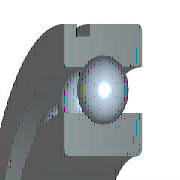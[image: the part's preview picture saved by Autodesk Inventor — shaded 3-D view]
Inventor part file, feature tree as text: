
AUTODESK INVENTOR PART (.ipt)
format: ipt  version: 2015 (Build 190159000, 159)  size: 336,384 bytes
history: native  units: mm (DEFAULTED — no unit token found)
features: sketch x1, other x1, pattern_circular x1
ambient origin geometry x8: Origin, YZ Plane, XZ Plane, XY Plane, X Axis, Y Axis, Z Axis, Center Point
bodies: Solid1 (feature_tree)
feature tree (3):
  sketch  "草图"  dims[d0=4.42mm d17=90.0deg d18=90.0deg d1=0.3mm d2=100.0mm d3=360.0deg d4=0.0mm d5=0.0mm d6=0.0mm d7=20.0mm d8=37.0mm d9=28.5mm d10=35.92mm d11=25.542mm d12=25.542mm d13=25.542mm d14=0.0mm d15=9.0mm d16=9.0mm d19=1.5mm d20=3.0mm d22=4.5mm d23=0.0mm d24=0.0mm]
  other  "轴承体"
  pattern_circular  "IDS_ARRAYBALL[SIMPL:T]"  Angle=90.0deg  [1 undecoded]
note: 1 required parameter value undecoded (feature->parameter linkage not recoverable at this tier; creation-order binding heuristic only, values carry confidence <= 0.55)
